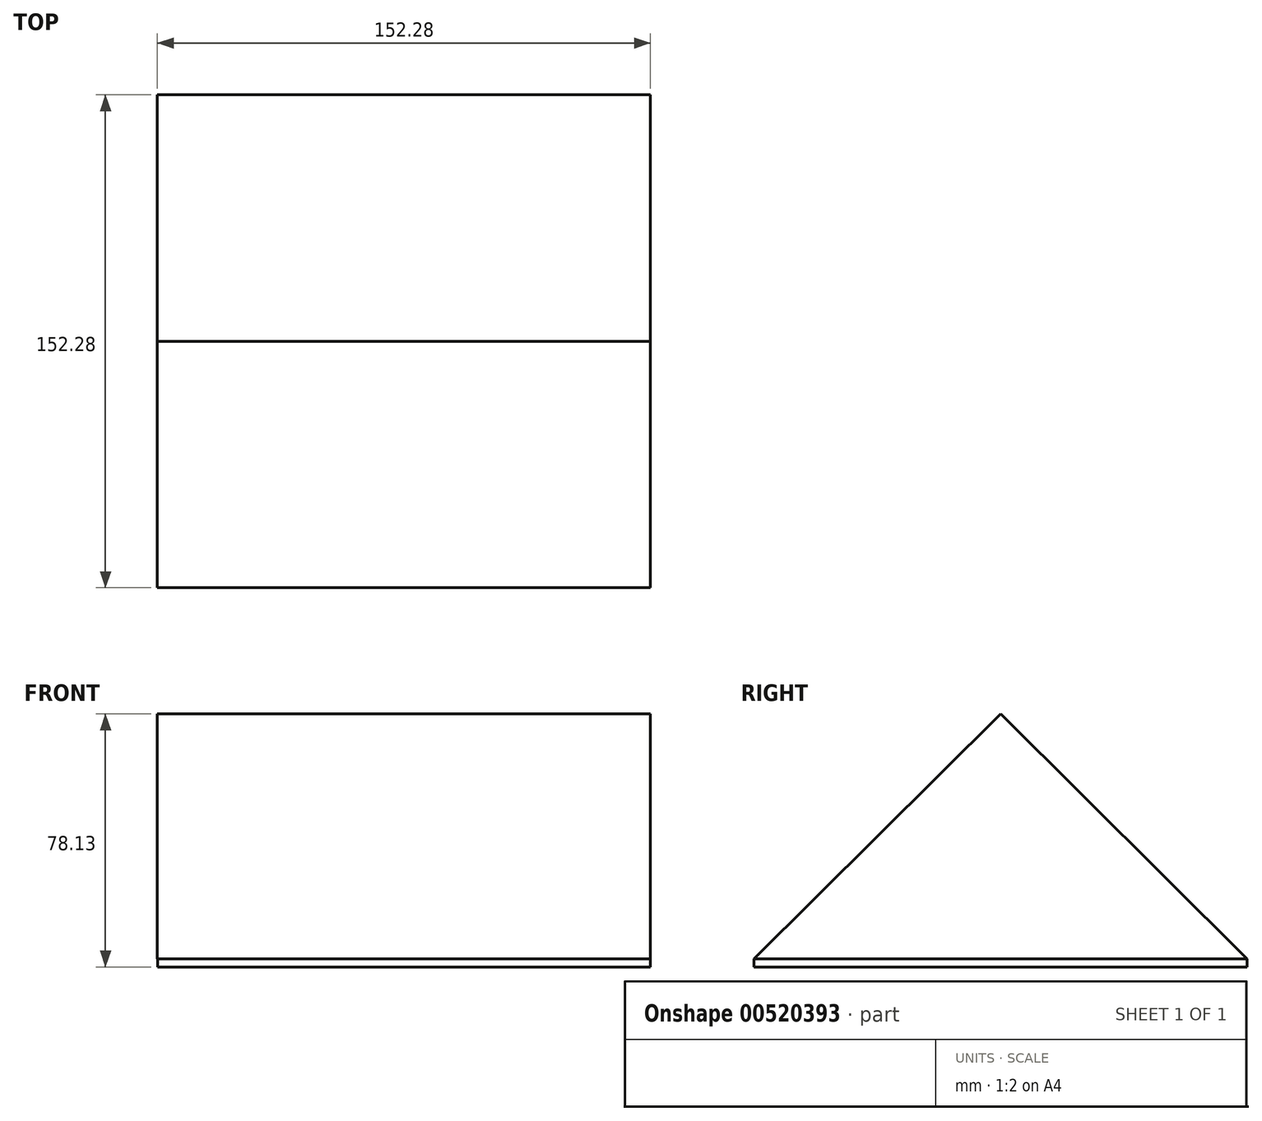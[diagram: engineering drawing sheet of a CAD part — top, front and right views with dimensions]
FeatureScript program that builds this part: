
annotation { "Feature Type Name" : "Feature", "Feature Type Description" : "" }
export const myFeature = defineFeature(function(context is Context, id is Id, definition is map)
    precondition{}
    {
        {
            var Q0;
            Q0=qCreatedBy(makeId("Top.planeOp"),FACE);
            var sketch = newSketch(context, id + "F0", { "sketchPlane" : qUnion([Q0])});
            skLineSegment(sketch, "E0", {"start": v(0, 0) * mm, "end": v(0, 76.14) * mm});
            skLineSegment(sketch, "E1", {"start": v(0, 0) * mm, "end": v(0, -76.14) * mm});
            skLineSegment(sketch, "E2", {"start": v(0, -76.14) * mm, "end": v(-76.02, -76.14) * mm});
            skLineSegment(sketch, "E3", {"start": v(-76.02, -76.14) * mm, "end": v(-76.02, 0) * mm});
            skLineSegment(sketch, "E4", {"start": v(-76.02, 0) * mm, "end": v(-76.02, 76.14) * mm});
            skLineSegment(sketch, "E5", {"start": v(-76.02, 76.14) * mm, "end": v(0, 76.14) * mm});
            skLineSegment(sketch, "E6", {"start": v(-76.02, 0) * mm, "end": v(0, 0) * mm});
            skLineSegment(sketch, "E7.MirrorCS", {"start": v(76.02, 0) * mm, "end": v(76.02, 76.14) * mm});
            skLineSegment(sketch, "E8.MirrorCS", {"start": v(76.02, 76.14) * mm, "end": v(0, 76.14) * mm});
            skLineSegment(sketch, "E9.MirrorCS", {"start": v(0, -76.14) * mm, "end": v(76.02, -76.14) * mm});
            skLineSegment(sketch, "E10.MirrorCS", {"start": v(76.02, -76.14) * mm, "end": v(76.02, 0) * mm});
            skLineSegment(sketch, "E11.MirrorCS", {"start": v(76.02, 0) * mm, "end": v(0, 0) * mm});
            skSolve(sketch);
        }
        {
            var Q0;
            Q0 = qSketchRegion(id + "F0", true);
            extrude(context, id + "F1", {"entities" : qUnion([Q0]), "depth" : 2.54 * mm, "offsetDistance" : 25.4 * mm});
        }
        {
            var Q0;
            Q0=qCreatedBy(makeId("Right.planeOp"),FACE);
            var sketch = newSketch(context, id + "F2", { "sketchPlane" : qUnion([Q0])});
            skLineSegment(sketch, "E12.0", {"start": v(-76.14, 2.54) * mm, "end": v(76.14, 2.54) * mm});
            skLineSegment(sketch, "E13", {"start": v(-76.14, 2.54) * mm, "end": v(0, 78.13) * mm});
            skLineSegment(sketch, "E14", {"start": v(0, 78.13) * mm, "end": v(76.14, 2.54) * mm});
            skSolve(sketch);
        }
        {
            var Q0;
            Q0 = qSketchRegion(id + "F2", true);
            extrude(context, id + "F3", {"entities" : qUnion([Q0]), "operationType" : NewBodyOperationType.ADD, "endBound" : BoundingType.SYMMETRIC, "depth" : 152.27 * mm, "offsetDistance" : 25.4 * mm});
        }
    });
